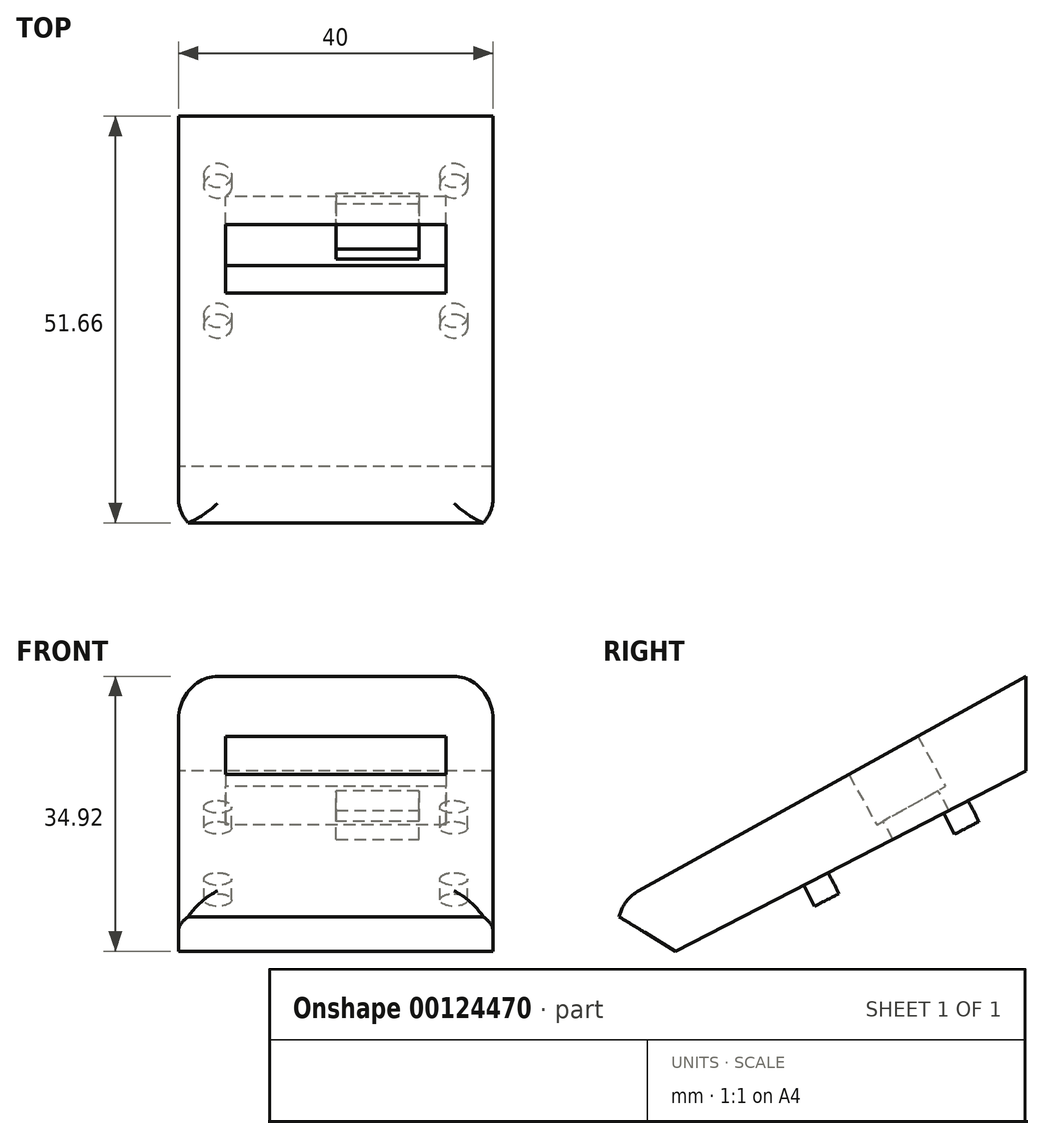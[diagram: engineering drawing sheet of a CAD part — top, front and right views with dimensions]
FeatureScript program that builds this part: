
annotation { "Feature Type Name" : "Feature", "Feature Type Description" : "" }
export const myFeature = defineFeature(function(context is Context, id is Id, definition is map)
    precondition{}
    {
        {
            var Q0;
            Q0=qCreatedBy(makeId("Right.planeOp"),FACE);
            var sketch = newSketch(context, id + "F0", { "sketchPlane" : qUnion([Q0])});
            skLineSegment(sketch, "E0", {"start": v(15.7, 17.9) * mm, "end": v(15.7, 5.9) * mm});
            skLineSegment(sketch, "E1", {"start": v(15.7, 5.9) * mm, "end": v(-36.07, -20.78) * mm});
            skLineSegment(sketch, "E2", {"start": v(-36.07, -20.78) * mm, "end": v(-36.07, -10.78) * mm});
            skLineSegment(sketch, "E3", {"start": v(-36.07, -10.78) * mm, "end": v(15.7, 17.9) * mm});
            skLineSegment(sketch, "E4", {"start": v(1.96, 10.28) * mm, "end": v(5.5, 3.9) * mm});
            skLineSegment(sketch, "E5", {"start": v(5.5, 3.9) * mm, "end": v(-3.25, -0.95) * mm});
            skLineSegment(sketch, "E6", {"start": v(-3.25, -0.95) * mm, "end": v(-6.79, 5.44) * mm});
            skSolve(sketch);
        }
        {
            var Q0;
            {var subQ3=sQuery(id+"F0.wireOp",EDGE,"E0");Q0=makeQuery(id+"F0.imprint","IMPRINT",FACE,{"disambiguationData":[TD([[makeQuery(id+"F0.imprint","IMPRINT",EDGE,{"derivedFrom":subQ3}),-1.0]])]});}
            extrude(context, id + "F1", {"entities" : qUnion([Q0]), "depth" : 40 * mm});
        }
        {
            var Q0;
            Q0=makeQuery(id+"F1.opExtrude","SWEPT_FACE",FACE,{"disambiguationData":[OSD([sQuery(id+"F0.wireOp",EDGE,"E4")])]});
            var sketch = newSketch(context, id + "F2", { "sketchPlane" : qUnion([Q0])});
            skLineSegment(sketch, "E7.bottom", {"start": v(0, 8.04) * mm, "end": v(6, 8.04) * mm});
            skLineSegment(sketch, "E7.top", {"start": v(0, 0.74) * mm, "end": v(6, 0.74) * mm});
            skLineSegment(sketch, "E7.left", {"start": v(0, 8.04) * mm, "end": v(0, 0.74) * mm});
            skLineSegment(sketch, "E7.right", {"start": v(6, 8.04) * mm, "end": v(6, 0.74) * mm});
            skLineSegment(sketch, "E8.bottom", {"start": v(40, 8.04) * mm, "end": v(34, 8.04) * mm});
            skLineSegment(sketch, "E8.top", {"start": v(40, 0.74) * mm, "end": v(34, 0.74) * mm});
            skLineSegment(sketch, "E8.left", {"start": v(40, 8.04) * mm, "end": v(40, 0.74) * mm});
            skLineSegment(sketch, "E8.right", {"start": v(34, 8.04) * mm, "end": v(34, 0.74) * mm});
            skSolve(sketch);
        }
        {
            var Q0;
            Q0=makeQuery(id+"F2.imprint","IMPRINT",FACE,{"disambiguationData":[TD([[makeQuery(id+"F2.imprint","IMPRINT",EDGE,{"derivedFrom":sQuery(id+"F2.wireOp",EDGE,"E7.bottom")}),1.0]])]});
            var Q1;
            Q1=makeQuery(id+"F2.imprint","IMPRINT",FACE,{"disambiguationData":[TD([[makeQuery(id+"F2.imprint","IMPRINT",EDGE,{"derivedFrom":sQuery(id+"F2.wireOp",EDGE,"E8.bottom")}),1.0]])]});
            extrude(context, id + "F3", {"entities" : qUnion([Q0, Q1]), "operationType" : NewBodyOperationType.ADD, "endBound" : BoundingType.UP_TO_NEXT, "depth" : 25 * mm});
        }
        {
            var Q0;
            Q0=makeQuery(id+"F1.opExtrude","SWEPT_FACE",FACE,{"disambiguationData":[OSD([sQuery(id+"F0.wireOp",EDGE,"E5")])]});
            var sketch = newSketch(context, id + "F4", { "sketchPlane" : qUnion([Q0])});
            skLineSegment(sketch, "E9.bottom", {"start": v(30.56, 5.6) * mm, "end": v(20.06, 5.6) * mm});
            skLineSegment(sketch, "E9.top", {"start": v(30.56, -2.4) * mm, "end": v(20.06, -2.4) * mm});
            skLineSegment(sketch, "E9.left", {"start": v(30.56, 5.6) * mm, "end": v(30.56, -2.4) * mm});
            skLineSegment(sketch, "E9.right", {"start": v(20.06, 5.6) * mm, "end": v(20.06, -2.4) * mm});
            skSolve(sketch);
        }
        {
            var Q0;
            Q0 = qSketchRegion(id + "F4", true);
            extrude(context, id + "F5", {"entities" : qUnion([Q0]), "operationType" : NewBodyOperationType.REMOVE, "oppositeDirection" : true, "depth" : 25 * mm});
        }
        {
            var Q0;
            Q0=makeQuery(id+"F1.opExtrude","SWEPT_FACE",FACE,{"disambiguationData":[OSD([sQuery(id+"F0.wireOp",EDGE,"E1")])]});
            var sketch = newSketch(context, id + "F6", { "sketchPlane" : qUnion([Q0])});
            skLineSegment(sketch, "E10", {"start": v(35, -16.66) * mm, "end": v(35, 41.59) * mm, "construction": true});
            skLineSegment(sketch, "E11", {"start": v(5, -16.66) * mm, "end": v(5, 41.59) * mm, "construction": true});
            skCircle(sketch, "E12", {"center": v(35, -6.66) * mm, "radius": 1.75 * mm});
            skCircle(sketch, "E13", {"center": v(5, -6.66) * mm, "radius": 1.75 * mm});
            skCircle(sketch, "E14", {"center": v(35, 13.34) * mm, "radius": 1.75 * mm});
            skCircle(sketch, "E15", {"center": v(5, 13.34) * mm, "radius": 1.75 * mm});
            skSolve(sketch);
        }
        {
            var Q0;
            Q0 = qSketchRegion(id + "F6", true);
            extrude(context, id + "F7", {"entities" : qUnion([Q0]), "operationType" : NewBodyOperationType.ADD, "depth" : 3 * mm});
        }
        {
            var Q0;
            Q0=makeQuery(id+"F1.opExtrude","SWEPT_EDGE",EDGE,{"disambiguationData":[OSD([sQuery(id+"F0.wireOp",EDGE,"E2"),sQuery(id+"F0.wireOp",EDGE,"E3")])]});
            var Q1;
            {var subQ0=sQuery(id+"F0.wireOp",EDGE,"E6");var subQ1=sQuery(id+"F0.wireOp",EDGE,"E3");Q1=makeQuery(id+"F3.boolean.opBoolean","MERGE",EDGE,{"derivedFrom":[makeQuery(id+"F1.opExtrude","CAP_EDGE",EDGE,{"disambiguationData":[OSD([subQ1]),TDD([makeQuery(id+"F0.imprint","IMPRINT",EDGE,{"disambiguationData":[TD([[makeQuery(id+"F0.imprint","INTERSECT",VERTEX,{"derivedFrom":[sQuery(id+"F0.wireOp",EDGE,"E2"),subQ1]}),-1.0]])],"derivedFrom":subQ1})])],"isStart":false}),makeQuery(id+"F1.opExtrude","CAP_EDGE",EDGE,{"disambiguationData":[OSD([subQ1]),TDD([makeQuery(id+"F0.imprint","IMPRINT",EDGE,{"disambiguationData":[TD([[makeQuery(id+"F0.imprint","INTERSECT",VERTEX,{"derivedFrom":[sQuery(id+"F0.wireOp",EDGE,"E0"),subQ1]}),1.0]])],"derivedFrom":subQ1})])],"isStart":false}),makeQuery(id+"F3.opExtrude","SWEPT_EDGE",EDGE,{"disambiguationData":[OSD([subQ1,subQ0])]})]});}
            var Q2;
            {var subQ0=sQuery(id+"F0.wireOp",EDGE,"E4");var subQ1=sQuery(id+"F0.wireOp",EDGE,"E3");Q2=makeQuery(id+"F3.boolean.opBoolean","MERGE",EDGE,{"derivedFrom":[makeQuery(id+"F1.opExtrude","CAP_EDGE",EDGE,{"disambiguationData":[OSD([subQ1]),TDD([makeQuery(id+"F0.imprint","IMPRINT",EDGE,{"disambiguationData":[TD([[makeQuery(id+"F0.imprint","INTERSECT",VERTEX,{"derivedFrom":[sQuery(id+"F0.wireOp",EDGE,"E2"),subQ1]}),-1.0]])],"derivedFrom":subQ1})])],"isStart":true}),makeQuery(id+"F1.opExtrude","CAP_EDGE",EDGE,{"disambiguationData":[OSD([subQ1]),TDD([makeQuery(id+"F0.imprint","IMPRINT",EDGE,{"disambiguationData":[TD([[makeQuery(id+"F0.imprint","INTERSECT",VERTEX,{"derivedFrom":[sQuery(id+"F0.wireOp",EDGE,"E0"),subQ1]}),1.0]])],"derivedFrom":subQ1})])],"isStart":true}),makeQuery(id+"F3.opExtrude","SWEPT_EDGE",EDGE,{"disambiguationData":[OSD([subQ1,subQ0,sQuery(id+"F2.wireOp",EDGE,"E7.bottom"),sQuery(id+"F2.wireOp",EDGE,"E7.left")])]})]});}
            fillet(context, id + "F8", {"entities" : qUnion([Q0, Q1, Q2]), "radius" : 5 * mm, "tangentPropagation" : true, "allowEdgeOverflow" : false});
        }
        {
            var Q0;
            Q0=makeQuery(id+"F1.opExtrude","SWEPT_EDGE",EDGE,{"disambiguationData":[OSD([sQuery(id+"F0.wireOp",EDGE,"E1"),sQuery(id+"F0.wireOp",EDGE,"E2")])]});
            chamfer(context, id + "F9", {"entities" : qUnion([Q0]), "width" : 5 * mm, "tangentPropagation" : true});
        }
    });
